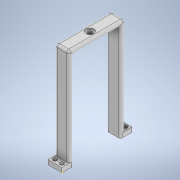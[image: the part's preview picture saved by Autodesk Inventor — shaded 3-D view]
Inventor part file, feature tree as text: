
AUTODESK INVENTOR PART (.ipt)
format: ipt  version: 2020 (Build 240168000, 168)  size: 221,696 bytes
history: native  units: in
note: dims shown in document units (in); Inventor stores cm internally (conversion verified against a paired STEP export)
features: sketch x8, extrude x5, hole x3, projected_geometry x3, fillet x1
ambient origin geometry x8: Origin, YZ Plane, XZ Plane, XY Plane, X Axis, Y Axis, Z Axis, Center Point
bodies: Solid1 (feature_tree)
feature tree (20):
  extrude  "Extrusion1"  Depth=0.375in
  hole  "Hole1"  [1 undecoded]
  hole  "Hole2"  [1 undecoded]
  sketch  "Sketch4"  dims[d4=0.0591in d5=0.75in d6=0.375in d7=0.25in d8=0.5635in d9=0.25in d10=0.8108in d11=0.188in]
  extrude  "Extrusion2"  Depth=3.05in
  extrude  "Extrusion3"  Depth=0.75in
  extrude  "Extrusion4"  Depth=0.125in
  extrude  "Extrusion5"  Depth=0.125in
  hole  "Hole3"  [1 undecoded]
  fillet  "Fillet2"  Radius=0.25in
  sketch  "Sketch1"  dims[d0=0.75in d1=0.375in]
  sketch  "Sketch2"  dims[d2=0.25in d3=0.0in]
  sketch  "Sketch5"  dims[d12=0.188in d13=0.188in]
  projected_geometry  "Projected Loop1"
  sketch  "Sketch6"  dims[d14=0.188in]
  projected_geometry  "Projected Loop2"
  sketch  "Sketch7"  dims[d15=0.129in d16=0.75in d17=0.219in d18=0.112in d19=0.5635in d20=0.25in d21=0.8108in d23=3.05in]
  sketch  "Sketch8"  dims[d24=90.0deg d25=0.75in]
  sketch  "Sketch9"  dims[d26=0.375in d27=0.188in d28=0.188in d29=0.188in d30=0.25in d31=0.0in d32=0.25in d33=0.0in d34=0.25in d35=0.25in d36=5.0in d37=0.0in d38=0.25in d39=0.0in d40=0.266in d41=0.75in d42=0.438in d43=0.0625in d44=0.5635in d45=1.0in d46=0.8108in d47=0.125in]
  projected_geometry  "Projected Loop3"
note: 3 required parameter values undecoded (feature->parameter linkage not recoverable at this tier; creation-order binding heuristic only, values carry confidence <= 0.55)
